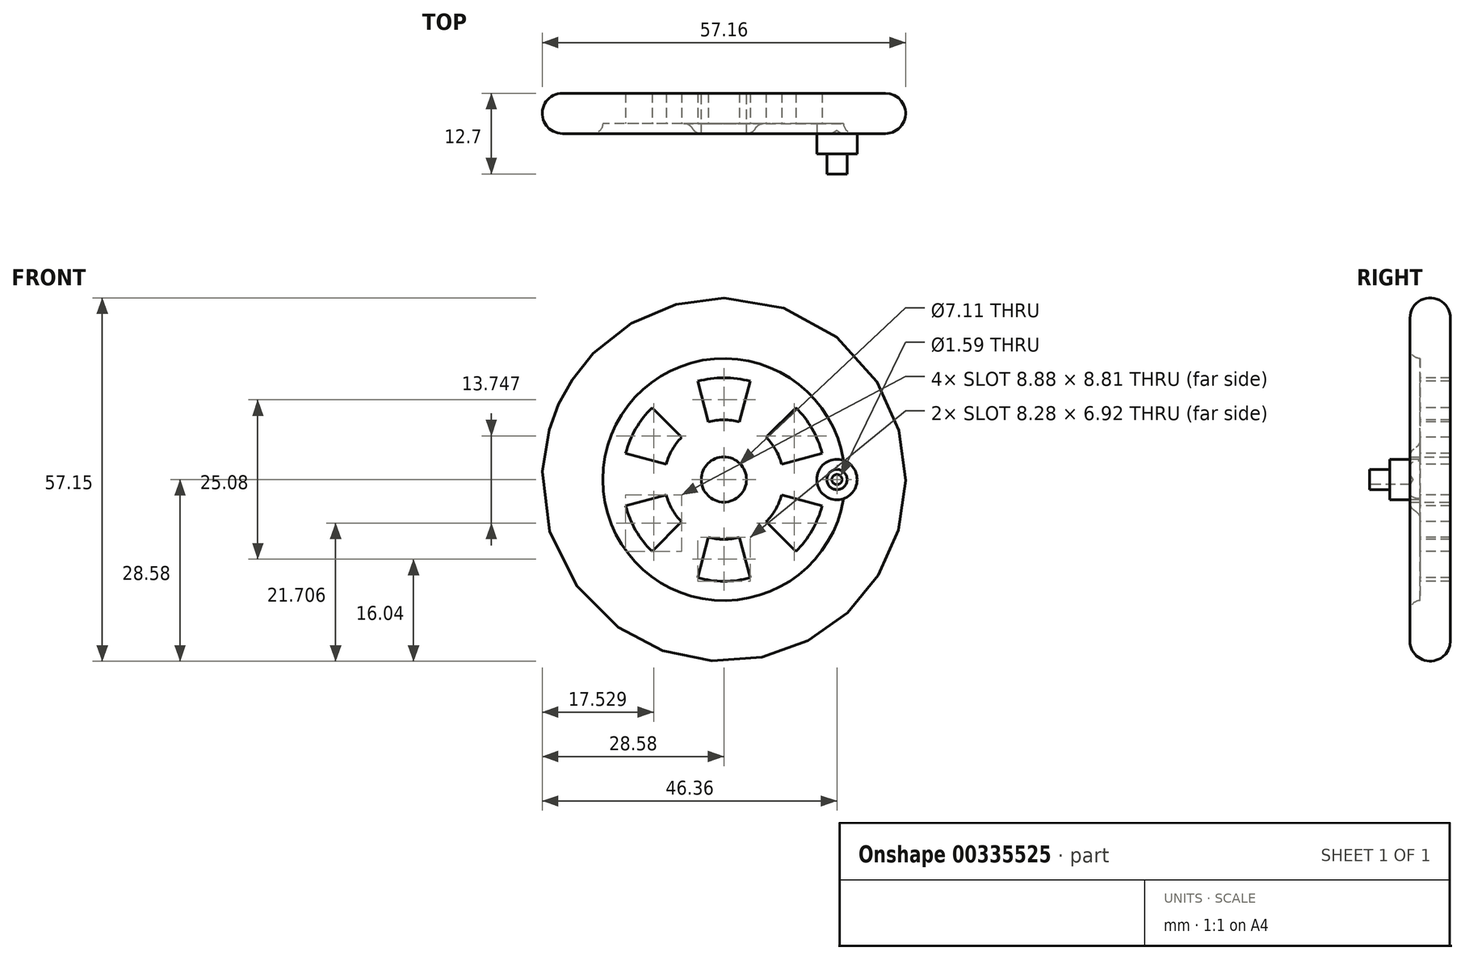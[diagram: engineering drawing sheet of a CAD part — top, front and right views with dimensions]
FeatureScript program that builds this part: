
annotation { "Feature Type Name" : "Feature", "Feature Type Description" : "" }
export const myFeature = defineFeature(function(context is Context, id is Id, definition is map)
    precondition{}
    {
        {
            var Q0;
            Q0=qCreatedBy(makeId("Top.planeOp"),FACE);
            var sketch = newSketch(context, id + "F0", { "sketchPlane" : qUnion([Q0])});
            skLineSegment(sketch, "E0", {"start": v(0, 0) * mm, "end": v(-3.56, 0) * mm, "construction": true});
            skLineSegment(sketch, "E1", {"start": v(-3.56, 0) * mm, "end": v(-25.4, 0) * mm});
            skArc(sketch, "E2", {"start": v(-25.4, 0) * mm, "mid": v(-28.58, -3.18) * mm, "end": v(-25.4, -6.35) * mm});
            skLineSegment(sketch, "E3", {"start": v(-25.4, 0) * mm, "end": v(-25.4, -6.35) * mm, "construction": true});
            skLineSegment(sketch, "E4", {"start": v(-3.56, 0) * mm, "end": v(-3.56, -6.35) * mm});
            skLineSegment(sketch, "E5", {"start": v(-3.56, -6.35) * mm, "end": v(-3.56, -4.75) * mm, "construction": true});
            skArc(sketch, "E6", {"start": v(-5.16, -4.75) * mm, "mid": v(-4.69, -5.88) * mm, "end": v(-3.56, -6.35) * mm});
            skLineSegment(sketch, "E7", {"start": v(-3.56, -4.75) * mm, "end": v(-5.16, -4.75) * mm, "construction": true});
            skLineSegment(sketch, "E8", {"start": v(-5.16, -4.75) * mm, "end": v(-19.05, -4.75) * mm});
            skLineSegment(sketch, "E9", {"start": v(-20.65, -6.35) * mm, "end": v(-25.4, -6.35) * mm});
            skLineSegment(sketch, "E10", {"start": v(-19.05, -4.75) * mm, "end": v(-20.65, -4.75) * mm, "construction": true});
            skLineSegment(sketch, "E11", {"start": v(-20.65, -4.75) * mm, "end": v(-20.65, -6.35) * mm, "construction": true});
            skCircle(sketch, "E12", {"center": v(-20.65, -4.75) * mm, "radius": 1.6 * mm});
            skLineSegment(sketch, "E13", {"start": v(0, 0) * mm, "end": v(0, -6.26) * mm, "construction": true});
            skSolve(sketch);
        }
        {
            var Q0;
            Q0=makeQuery(id+"F0.imprint","IMPRINT",FACE,{"disambiguationData":[TD([[makeQuery(id+"F0.imprint","IMPRINT",EDGE,{"derivedFrom":sQuery(id+"F0.wireOp",EDGE,"E1")}),1.0]])]});
            var Q1;
            {var subQ0=sQuery(id+"F0.wireOp",EDGE,"E12");var subQ1=makeQuery(id+"F0.imprint","INTERSECT",VERTEX,{"derivedFrom":[sQuery(id+"F0.wireOp",EDGE,"E8"),subQ0]});Q1=makeQuery(id+"F0.imprint","IMPRINT",FACE,{"disambiguationData":[TD([[makeQuery(id+"F0.imprint","IMPRINT",EDGE,{"disambiguationData":[TD([[subQ1,-1.0]])],"derivedFrom":subQ0}),1.0]])]});}
            var Q2;
            Q2=sQuery(id+"F0.wireOp",EDGE,"E13");
            revolve(context, id + "F1", {"entities" : qUnion([Q0, Q1]), "axis" : qUnion([Q2]), "revolveType" : RevolveType.FULL});
        }
        {
            var Q0;
            Q0=makeQuery(id+"F1.opRevolve","SWEPT_EDGE",EDGE,{"disambiguationData":[OSD([sQuery(id+"F0.wireOp",EDGE,"E6"),sQuery(id+"F0.wireOp",EDGE,"E8")])]});
            fillet(context, id + "F2", {"entities" : qUnion([Q0]), "radius" : 1.6 * mm, "tangentPropagation" : true, "allowEdgeOverflow" : false});
        }
        {
            var Q0;
            Q0=makeQuery(id+"F1.opRevolve","SWEPT_FACE",FACE,{"disambiguationData":[OSD([sQuery(id+"F0.wireOp",EDGE,"E8")])]});
            var sketch = newSketch(context, id + "F3", { "sketchPlane" : qUnion([Q0])});
            skArc(sketch, "E14", {"start": v(2.43, 9.08) * mm, "mid": v(0, 9.4) * mm, "end": v(-2.43, 9.08) * mm});
            skArc(sketch, "E15", {"start": v(4.14, 15.46) * mm, "mid": v(0, 16) * mm, "end": v(-4.14, 15.46) * mm});
            skLineSegment(sketch, "E16", {"start": v(0, 0) * mm, "end": v(0, 16) * mm, "construction": true});
            skLineSegment(sketch, "E17", {"start": v(2.43, 9.08) * mm, "end": v(4.14, 15.46) * mm});
            skLineSegment(sketch, "E18", {"start": v(-2.43, 9.08) * mm, "end": v(-4.14, 15.46) * mm});
            skLineSegment(sketch, "E19.1.0", {"start": v(-9.08, -2.43) * mm, "end": v(-15.46, -4.14) * mm});
            skArc(sketch, "E19.1.1", {"start": v(-15.46, -4.14) * mm, "mid": v(-13.86, -8) * mm, "end": v(-11.32, -11.32) * mm});
            skLineSegment(sketch, "E19.1.2", {"start": v(-6.65, -6.65) * mm, "end": v(-11.32, -11.32) * mm});
            skArc(sketch, "E19.1.3", {"start": v(-9.08, -2.43) * mm, "mid": v(-8.14, -4.7) * mm, "end": v(-6.65, -6.65) * mm});
            skLineSegment(sketch, "E19.2.0", {"start": v(6.65, -6.65) * mm, "end": v(11.32, -11.32) * mm});
            skArc(sketch, "E19.2.1", {"start": v(11.32, -11.32) * mm, "mid": v(13.86, -8) * mm, "end": v(15.46, -4.14) * mm});
            skLineSegment(sketch, "E19.2.2", {"start": v(9.08, -2.43) * mm, "end": v(15.46, -4.14) * mm});
            skArc(sketch, "E19.2.3", {"start": v(6.65, -6.65) * mm, "mid": v(8.14, -4.7) * mm, "end": v(9.08, -2.43) * mm});
            skLineSegment(sketch, "E20", {"start": v(0, 0) * mm, "end": v(-25.15, 0) * mm, "construction": true});
            skLineSegment(sketch, "E21.MirrorCS", {"start": v(-2.43, -9.08) * mm, "end": v(-4.14, -15.46) * mm});
            skArc(sketch, "E22.MirrorCS", {"start": v(2.43, -9.08) * mm, "mid": v(0, -9.4) * mm, "end": v(-2.43, -9.08) * mm});
            skArc(sketch, "E23.MirrorCS", {"start": v(4.14, -15.46) * mm, "mid": v(0, -16) * mm, "end": v(-4.14, -15.46) * mm});
            skLineSegment(sketch, "E24.MirrorCS", {"start": v(2.43, -9.08) * mm, "end": v(4.14, -15.46) * mm});
            skLineSegment(sketch, "E25.1.0", {"start": v(9.08, 2.43) * mm, "end": v(15.46, 4.14) * mm});
            skArc(sketch, "E25.1.1", {"start": v(6.65, 6.65) * mm, "mid": v(8.14, 4.7) * mm, "end": v(9.08, 2.43) * mm});
            skLineSegment(sketch, "E25.1.2", {"start": v(6.65, 6.65) * mm, "end": v(11.32, 11.32) * mm});
            skArc(sketch, "E25.1.3", {"start": v(11.32, 11.32) * mm, "mid": v(13.86, 8) * mm, "end": v(15.46, 4.14) * mm});
            skLineSegment(sketch, "E25.2.0", {"start": v(-6.65, 6.65) * mm, "end": v(-11.32, 11.32) * mm});
            skArc(sketch, "E25.2.1", {"start": v(-9.08, 2.43) * mm, "mid": v(-8.14, 4.7) * mm, "end": v(-6.65, 6.65) * mm});
            skLineSegment(sketch, "E25.2.2", {"start": v(-9.08, 2.43) * mm, "end": v(-15.46, 4.14) * mm});
            skArc(sketch, "E25.2.3", {"start": v(-15.46, 4.14) * mm, "mid": v(-13.86, 8) * mm, "end": v(-11.32, 11.32) * mm});
            skSolve(sketch);
        }
        {
            var Q0;
            Q0=makeQuery(id+"F3.imprint","IMPRINT",FACE,{"disambiguationData":[TD([[makeQuery(id+"F3.imprint","IMPRINT",EDGE,{"derivedFrom":sQuery(id+"F3.wireOp",EDGE,"E14")}),-1.0]])]});
            extrude(context, id + "F4", {"entities" : qUnion([Q0]), "operationType" : NewBodyOperationType.REMOVE, "oppositeDirection" : true, "depth" : 25.4 * mm});
        }
        {
            var Q0;
            Q0=makeQuery(id+"F3.imprint","IMPRINT",FACE,{"disambiguationData":[TD([[makeQuery(id+"F3.imprint","IMPRINT",EDGE,{"derivedFrom":sQuery(id+"F3.wireOp",EDGE,"E25.2.0")}),1.0]])]});
            var Q1;
            Q1=makeQuery(id+"F3.imprint","IMPRINT",FACE,{"disambiguationData":[TD([[makeQuery(id+"F3.imprint","IMPRINT",EDGE,{"derivedFrom":sQuery(id+"F3.wireOp",EDGE,"E25.1.0")}),1.0]])]});
            var Q2;
            Q2=makeQuery(id+"F3.imprint","IMPRINT",FACE,{"disambiguationData":[TD([[makeQuery(id+"F3.imprint","IMPRINT",EDGE,{"derivedFrom":sQuery(id+"F3.wireOp",EDGE,"E19.2.0")}),1.0]])]});
            var Q3;
            Q3=makeQuery(id+"F3.imprint","IMPRINT",FACE,{"disambiguationData":[TD([[makeQuery(id+"F3.imprint","IMPRINT",EDGE,{"derivedFrom":sQuery(id+"F3.wireOp",EDGE,"E21.MirrorCS")}),1.0]])]});
            var Q4;
            Q4=makeQuery(id+"F3.imprint","IMPRINT",FACE,{"disambiguationData":[TD([[makeQuery(id+"F3.imprint","IMPRINT",EDGE,{"derivedFrom":sQuery(id+"F3.wireOp",EDGE,"E19.1.0")}),1.0]])]});
            extrude(context, id + "F5", {"entities" : qUnion([Q0, Q1, Q2, Q3, Q4]), "operationType" : NewBodyOperationType.REMOVE, "oppositeDirection" : true, "depth" : 25.4 * mm});
        }
        {
            var Q0;
            Q0=makeQuery(id+"F1.opRevolve","SWEPT_FACE",FACE,{"disambiguationData":[OSD([sQuery(id+"F0.wireOp",EDGE,"E9")])]});
            var sketch = newSketch(context, id + "F6", { "sketchPlane" : qUnion([Q0])});
            skLineSegment(sketch, "E26", {"start": v(0, 0) * mm, "end": v(17.78, 0) * mm, "construction": true});
            skCircle(sketch, "E27", {"center": v(17.78, 0) * mm, "radius": 3.18 * mm});
            skSolve(sketch);
        }
        {
            var Q0;
            Q0 = qSketchRegion(id + "F6", true);
            extrude(context, id + "F7", {"entities" : qUnion([Q0]), "operationType" : NewBodyOperationType.ADD, "oppositeDirection" : true, "depth" : 5.08 * mm});
        }
        {
            var Q0;
            {var subQ0=sQuery(id+"F6.wireOp",EDGE,"E27");var subQ1=makeQuery(id+"F1.opRevolve","SWEPT_EDGE",EDGE,{"disambiguationData":[OSD([sQuery(id+"F0.wireOp",EDGE,"E9"),sQuery(id+"F0.wireOp",EDGE,"E12")])]});var subQ2=makeQuery(id+"F6.imprint","INTERSECT",VERTEX,{"disambiguationData":[OD(0.0)],"derivedFrom":[subQ1,subQ0]});Q0=makeQuery(id+"F6.imprint","IMPRINT",FACE,{"disambiguationData":[TD([[makeQuery(id+"F6.imprint","IMPRINT",EDGE,{"disambiguationData":[TD([[subQ2,-1.0]])],"derivedFrom":subQ0}),1.0]])]});}
            var Q1;
            {var subQ0=sQuery(id+"F6.wireOp",EDGE,"E27");var subQ1=makeQuery(id+"F1.opRevolve","SWEPT_EDGE",EDGE,{"disambiguationData":[OSD([sQuery(id+"F0.wireOp",EDGE,"E9"),sQuery(id+"F0.wireOp",EDGE,"E12")])]});var subQ2=makeQuery(id+"F6.imprint","INTERSECT",VERTEX,{"disambiguationData":[OD(0.0)],"derivedFrom":[subQ1,subQ0]});Q1=makeQuery(id+"F6.imprint","IMPRINT",FACE,{"disambiguationData":[TD([[makeQuery(id+"F6.imprint","IMPRINT",EDGE,{"disambiguationData":[TD([[subQ2,1.0]])],"derivedFrom":subQ0}),1.0]])]});}
            extrude(context, id + "F8", {"entities" : qUnion([Q0, Q1]), "operationType" : NewBodyOperationType.ADD, "depth" : 3.17 * mm});
        }
        {
            var Q0;
            Q0=makeQuery(id+"F8.opExtrude","CAP_FACE",FACE,{"disambiguationData":[OSD([sQuery(id+"F6.wireOp",EDGE,"E27")])],"isStart":false});
            var sketch = newSketch(context, id + "F9", { "sketchPlane" : qUnion([Q0])});
            skCircle(sketch, "E28", {"center": v(17.78, 0) * mm, "radius": 1.59 * mm});
            skSolve(sketch);
        }
        {
            var Q0;
            Q0 = qSketchRegion(id + "F9", true);
            extrude(context, id + "F10", {"entities" : qUnion([Q0]), "operationType" : NewBodyOperationType.ADD, "depth" : 3.17 * mm});
        }
        {
            var Q0;
            Q0=makeQuery(id+"F10.opExtrude","CAP_FACE",FACE,{"disambiguationData":[OSD([sQuery(id+"F9.wireOp",EDGE,"E28")])],"isStart":false});
            var sketch = newSketch(context, id + "F11", { "sketchPlane" : qUnion([Q0])});
            skPoint(sketch, "E29", {"position": v(17.78, 0) * mm});
            skSolve(sketch);
        }
        {
            var Q0;
            Q0=sQuery(id+"F11.wireOp",VERTEX,"E29");
            var Q1;
            Q1=makeQuery(id+"F1.opRevolve","SWEPT_BODY",BODY,{"disambiguationData":[OSD([sQuery(id+"F0.wireOp",EDGE,"E1"),sQuery(id+"F0.wireOp",EDGE,"E2"),sQuery(id+"F0.wireOp",EDGE,"E4"),sQuery(id+"F0.wireOp",EDGE,"E6"),sQuery(id+"F0.wireOp",EDGE,"E8"),sQuery(id+"F0.wireOp",EDGE,"E9"),sQuery(id+"F0.wireOp",EDGE,"E12")])]});
            hole(context, id + "F12", {"style" : HoleStyle.SIMPLE, "endStyle" : HoleEndStyle.BLIND, "holeDiameter" : 1.59 * mm, "holeDepth" : 6.35 * mm, "tappedDepth" : 12.7 * mm, "tapClearance" : 3, "locations" : qUnion([Q0]), "scope" : qUnion([Q1])});
        }
    });
